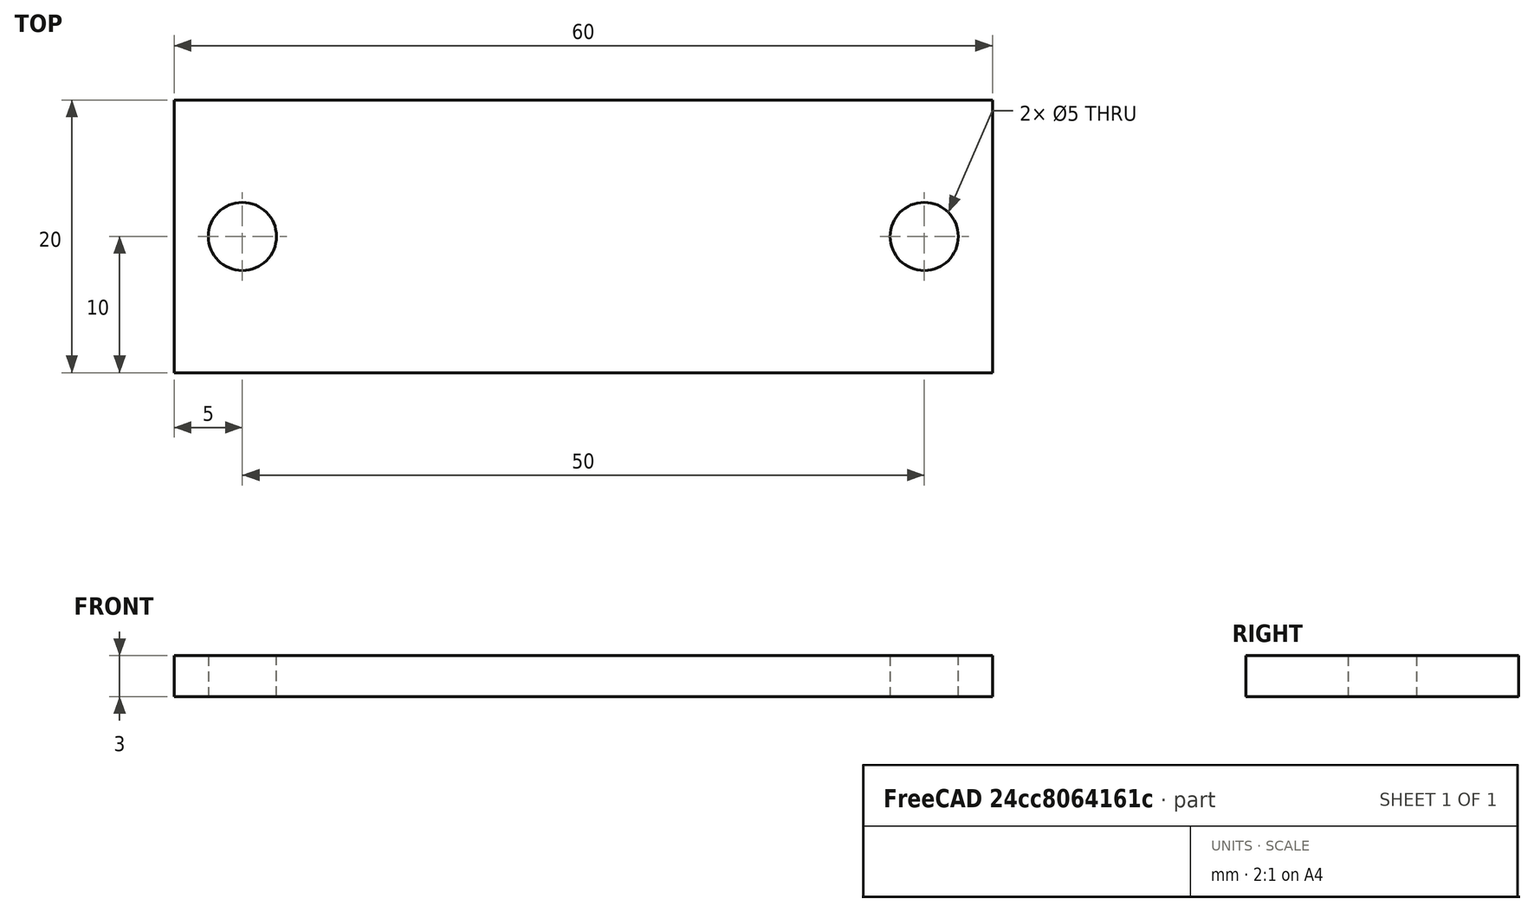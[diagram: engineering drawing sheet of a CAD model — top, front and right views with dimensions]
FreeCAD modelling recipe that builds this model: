
FCSTD DOCUMENT  (FreeCAD 0.16R6707 (Git))
Label: support bas tiges
License: All rights reserved
LicenseURL: http://en.wikipedia.org/wiki/All_rights_reserved
objects: Sketcher::SketchObject×1, PartDesign::Pad×1
note: 3 computed .brp shape members not serialized (recipe doc carries the construction recipe); baked Part::Feature solids carry a one-line shape summary decoded from their .brp

FEATURE [Sketcher::SketchObject] Sketch
  sketch-geometry (8):
    g0: LineSegment StartX=0 StartY=0 StartZ=0 EndX=60 EndY=0 EndZ=0
    g1: LineSegment StartX=60 StartY=0 StartZ=0 EndX=60 EndY=20 EndZ=0
    g2: LineSegment StartX=60 StartY=20 StartZ=0 EndX=0 EndY=20 EndZ=0
    g3: LineSegment StartX=0 StartY=20 StartZ=0 EndX=0 EndY=0 EndZ=0
    g4: GeomPoint [constr] X=5 Y=10 Z=0
    g5: GeomPoint [constr] X=55 Y=10 Z=0
    g6: Circle CenterX=5 CenterY=10 CenterZ=0 NormalX=0 NormalY=0 NormalZ=1 Radius=2.5
    g7: Circle CenterX=55 CenterY=10 CenterZ=0 NormalX=0 NormalY=0 NormalZ=1 Radius=2.5
  constraints (19):
    c: Coincident(g0,g1)
    c: Coincident(g1,g2)
    c: Coincident(g2,g3)
    c: Coincident(g3,g0)
    c: Horizontal(g0)
    c: Horizontal(g2)
    c: Vertical(g1)
    c: Vertical(g3)
    c: Coincident(g0,g-1)
    c: Distance(g1) = 20
    c: Distance(g2) = 60
    c: DistanceY(g5,g4) = 0
    c: DistanceX(g4,g5) = 50
    c: DistanceY(g-1,g4) = 10
    c: DistanceX(g-1,g4) = 5
    c: Coincident(g6,g4)
    c: Coincident(g7,g5)
    c: Radius(g6) = 2.5
    c: Radius(g7) = 2.5
FEATURE [PartDesign::Pad] Pad
  Length = 3
  Length2 = 100
  Sketch = -> Sketch
  Type = 0
